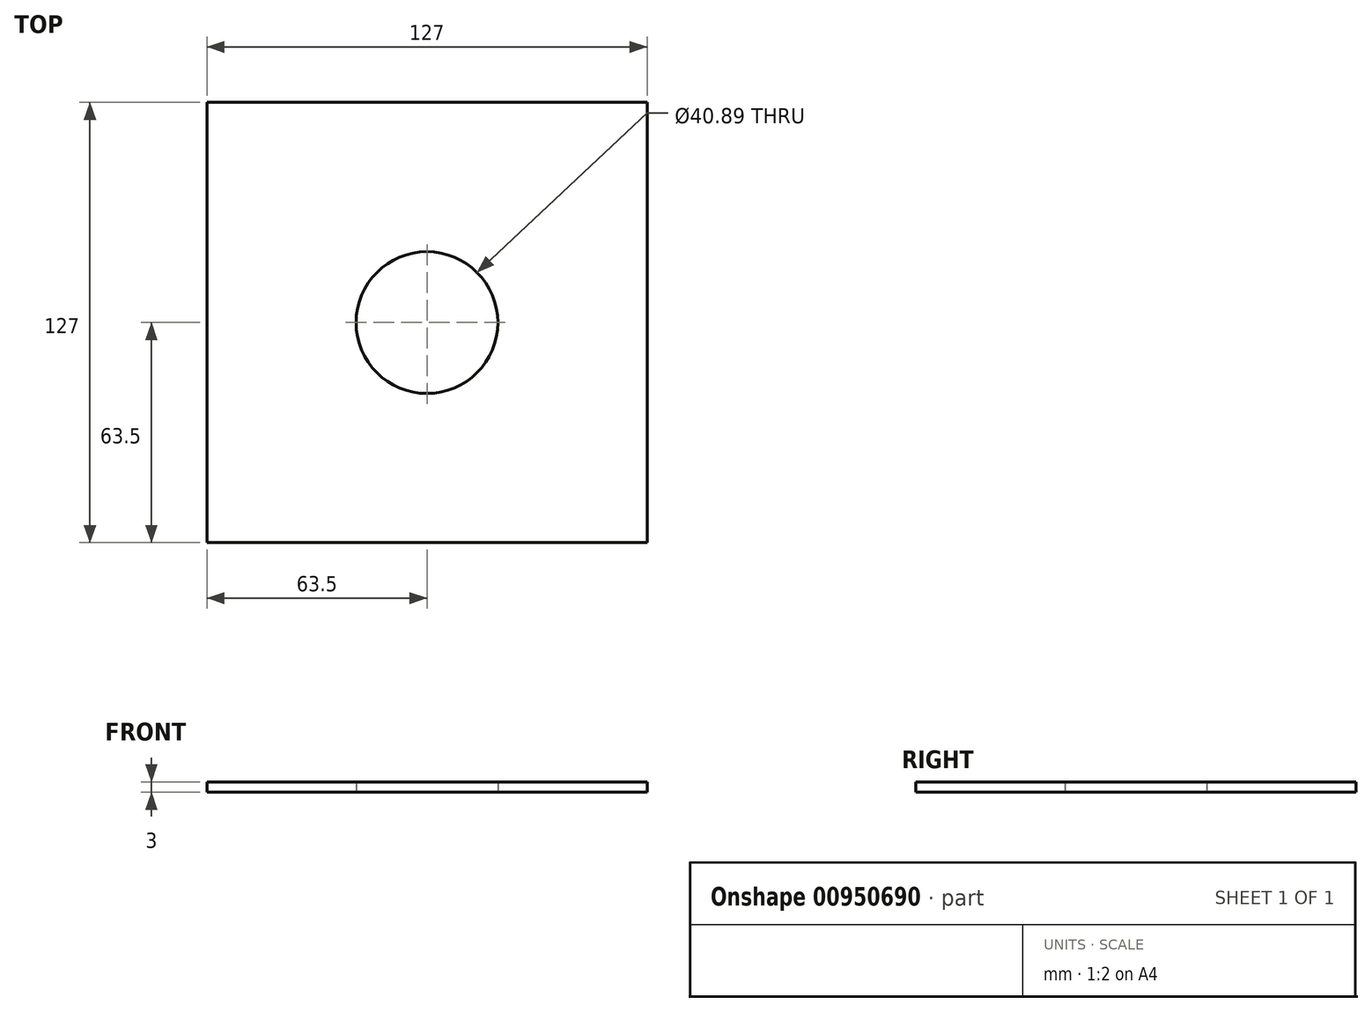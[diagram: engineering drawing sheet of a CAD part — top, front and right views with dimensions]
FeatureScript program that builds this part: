
annotation { "Feature Type Name" : "Feature", "Feature Type Description" : "" }
export const myFeature = defineFeature(function(context is Context, id is Id, definition is map)
    precondition{}
    {
        {
            var Q0;
            Q0=qCreatedBy(makeId("Top.planeOp"),FACE);
            var sketch = newSketch(context, id + "F0", { "sketchPlane" : qUnion([Q0])});
            skLineSegment(sketch, "E0.bottom", {"start": v(63.5, 63.5) * mm, "end": v(-63.5, 63.5) * mm});
            skLineSegment(sketch, "E0.top", {"start": v(63.5, -63.5) * mm, "end": v(-63.5, -63.5) * mm});
            skLineSegment(sketch, "E0.left", {"start": v(63.5, 63.5) * mm, "end": v(63.5, -63.5) * mm});
            skLineSegment(sketch, "E0.right", {"start": v(-63.5, 63.5) * mm, "end": v(-63.5, -63.5) * mm});
            skPoint(sketch, "E0.middle", {"position": v(0, 0) * mm});
            skCircle(sketch, "E1", {"center": v(0, 0) * mm, "radius": 20.45 * mm});
            skSolve(sketch);
        }
        {
            var Q0;
            Q0=makeQuery(id+"F0.imprint","IMPRINT",FACE,{"disambiguationData":[TD([[makeQuery(id+"F0.imprint","IMPRINT",EDGE,{"derivedFrom":sQuery(id+"F0.wireOp",EDGE,"E0.bottom")}),1.0]])]});
            extrude(context, id + "F1", {"entities" : qUnion([Q0]), "depth" : 3 * mm, "offsetDistance" : 25.4 * mm});
        }
    });
